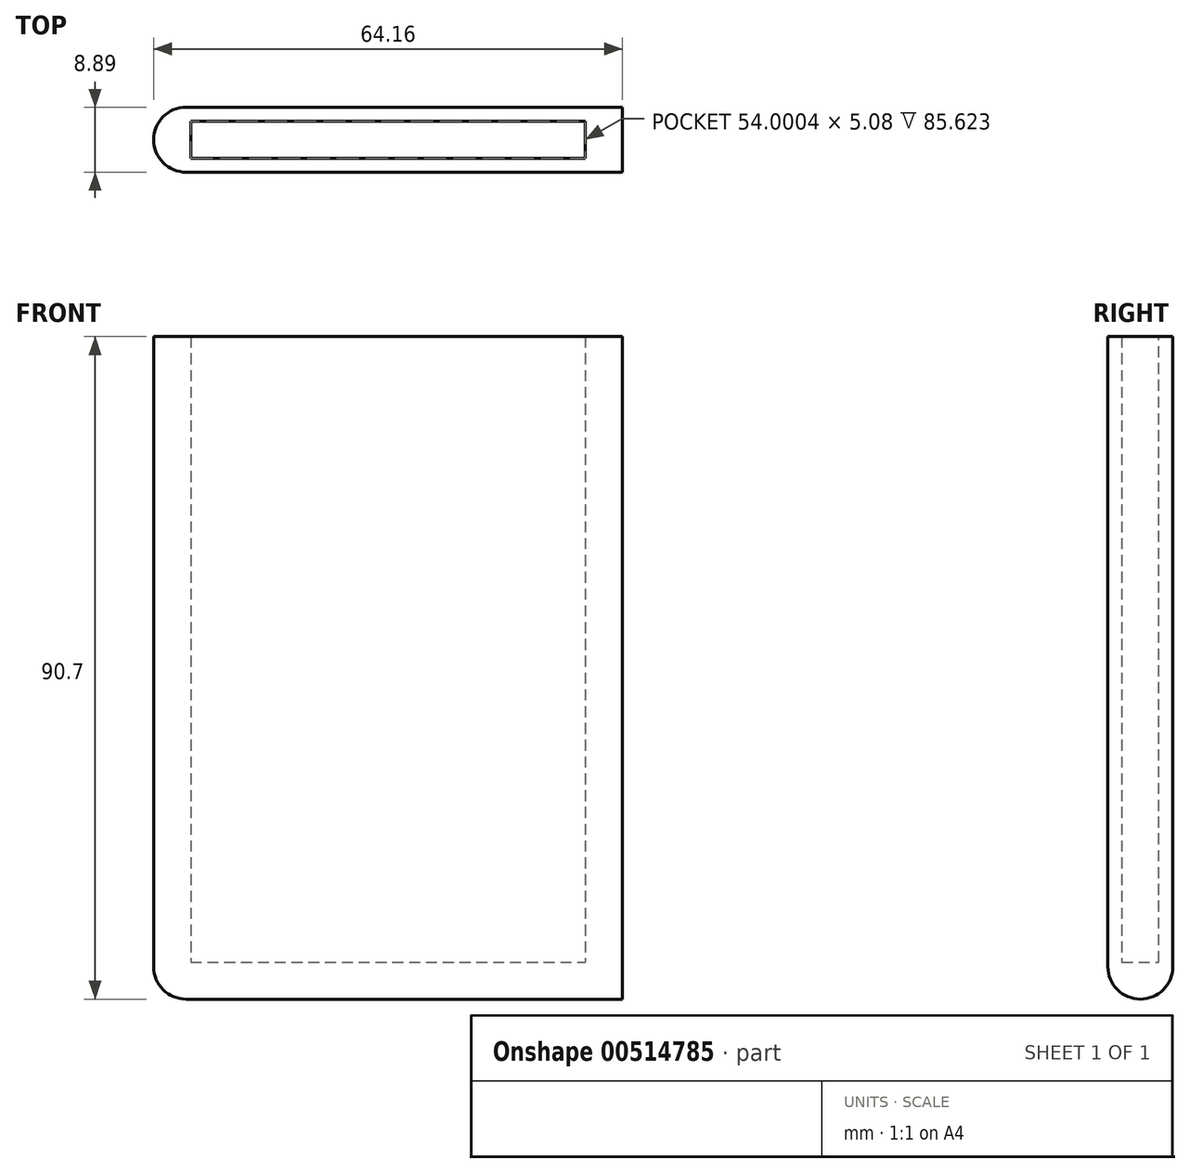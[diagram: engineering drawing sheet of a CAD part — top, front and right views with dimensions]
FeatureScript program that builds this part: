
annotation { "Feature Type Name" : "Feature", "Feature Type Description" : "" }
export const myFeature = defineFeature(function(context is Context, id is Id, definition is map)
    precondition{}
    {
        {
            var Q0;
            Q0=qCreatedBy(makeId("Front.planeOp"),FACE);
            var sketch = newSketch(context, id + "F0", { "sketchPlane" : qUnion([Q0])});
            skLineSegment(sketch, "E0.bottom", {"start": v(0, 0) * mm, "end": v(54, 0) * mm});
            skLineSegment(sketch, "E0.top", {"start": v(0, 85.62) * mm, "end": v(54, 85.62) * mm});
            skLineSegment(sketch, "E0.left", {"start": v(0, 0) * mm, "end": v(0, 85.62) * mm});
            skLineSegment(sketch, "E0.right", {"start": v(54, 0) * mm, "end": v(54, 85.62) * mm});
            skLineSegment(sketch, "E1.0", {"start": v(-5.08, 0) * mm, "end": v(-5.08, 85.62) * mm});
            skLineSegment(sketch, "E2.0", {"start": v(59.08, 0) * mm, "end": v(59.08, 85.62) * mm});
            skLineSegment(sketch, "E3.0", {"start": v(0, -5.08) * mm, "end": v(54, -5.08) * mm});
            skLineSegment(sketch, "E4.top", {"start": v(54, -5.08) * mm, "end": v(59.08, -5.08) * mm});
            skLineSegment(sketch, "E4.right", {"start": v(59.08, 0) * mm, "end": v(59.08, -5.08) * mm});
            skLineSegment(sketch, "E5.bottom", {"start": v(-5.08, 85.62) * mm, "end": v(59.08, 85.62) * mm});
            skLineSegment(sketch, "E5.top", {"start": v(-5.08, -5.08) * mm, "end": v(59.08, -5.08) * mm});
            skLineSegment(sketch, "E5.left", {"start": v(-5.08, 85.62) * mm, "end": v(-5.08, -5.08) * mm});
            skLineSegment(sketch, "E5.right", {"start": v(59.08, 85.62) * mm, "end": v(59.08, -5.08) * mm});
            skSolve(sketch);
        }
        {
            var Q0;
            Q0=makeQuery(id+"F0.imprint","IMPRINT",FACE,{"disambiguationData":[TD([[makeQuery(id+"F0.imprint","IMPRINT",EDGE,{"derivedFrom":sQuery(id+"F0.wireOp",EDGE,"E0.bottom")}),-1.0]])]});
            extrude(context, id + "F1", {"entities" : qUnion([Q0]), "depth" : 6.35 * mm, "offsetDistance" : 25.4 * mm});
        }
        {
            var Q0;
            Q0=makeQuery(id+"F1.opExtrude","CAP_FACE",FACE,{"disambiguationData":[OSD([sQuery(id+"F0.wireOp",EDGE,"E0.bottom"),sQuery(id+"F0.wireOp",EDGE,"E0.left"),sQuery(id+"F0.wireOp",EDGE,"E0.right"),sQuery(id+"F0.wireOp",EDGE,"E5.bottom"),sQuery(id+"F0.wireOp",EDGE,"E5.top"),sQuery(id+"F0.wireOp",EDGE,"E5.left"),sQuery(id+"F0.wireOp",EDGE,"E5.right")])],"isStart":false});
            extrude(context, id + "F2", {"entities" : qUnion([Q0]), "operationType" : NewBodyOperationType.ADD, "depth" : 1.27 * mm, "offsetDistance" : 25.4 * mm});
        }
        {
            var Q0;
            {var subQ0=sQuery(id+"F0.wireOp",EDGE,"E0.right");var subQ3=sQuery(id+"FsMvsPdMRP7UvRH_1.wireOp",EDGE,"BMKbSKOw-1y13-ICIE-zcvO-LVdtaucvQ7qD.top");Q0=makeQuery(id+"F2.boolean.opBoolean","MERGE",FACE,{"derivedFrom":[makeQuery(id+"FD6a4dajuMmCxVc_1.boolean.opBoolean","SPLIT",FACE,{"disambiguationData":[TD([makeQuery(id+"FD6a4dajuMmCxVc_1.opExtrude","SWEPT_FACE",FACE,{"disambiguationData":[OSD([subQ3])]})])],"derivedFrom":makeQuery(id+"F1.opExtrude","SWEPT_FACE",FACE,{"disambiguationData":[OSD([subQ0])]})}),makeQuery(id+"F2.opExtrude","SWEPT_FACE",FACE,{"disambiguationData":[OSD([subQ0])]})]});}
            var sketch = newSketch(context, id + "F3", { "sketchPlane" : qUnion([Q0])});
            skLineSegment(sketch, "E6.bottom", {"start": v(7.62, 85.62) * mm, "end": v(6.35, 85.62) * mm});
            skLineSegment(sketch, "E6.top", {"start": v(7.62, 0) * mm, "end": v(6.35, 0) * mm});
            skLineSegment(sketch, "E6.left", {"start": v(7.62, 85.62) * mm, "end": v(7.62, 0) * mm});
            skLineSegment(sketch, "E6.right", {"start": v(6.35, 85.62) * mm, "end": v(6.35, 0) * mm});
            skSolve(sketch);
        }
        {
            var Q0;
            Q0=makeQuery(id+"F3.imprint","IMPRINT",FACE,{"disambiguationData":[TD([[makeQuery(id+"F3.imprint","IMPRINT",EDGE,{"derivedFrom":sQuery(id+"F3.wireOp",EDGE,"E6.bottom")}),1.0]])]});
            extrude(context, id + "F4", {"entities" : qUnion([Q0]), "operationType" : NewBodyOperationType.ADD, "depth" : 54 * mm, "offsetDistance" : 25.4 * mm});
        }
        {
            var Q0;
            Q0=makeQuery(id+"F1.opExtrude","CAP_FACE",FACE,{"disambiguationData":[OSD([sQuery(id+"F0.wireOp",EDGE,"E0.bottom"),sQuery(id+"F0.wireOp",EDGE,"E0.left"),sQuery(id+"F0.wireOp",EDGE,"E0.right"),sQuery(id+"F0.wireOp",EDGE,"E5.bottom"),sQuery(id+"F0.wireOp",EDGE,"E5.top"),sQuery(id+"F0.wireOp",EDGE,"E5.left"),sQuery(id+"F0.wireOp",EDGE,"E5.right")])],"isStart":true});
            extrude(context, id + "F5", {"entities" : qUnion([Q0]), "operationType" : NewBodyOperationType.ADD, "depth" : 1.27 * mm, "offsetDistance" : 25.4 * mm});
        }
        {
            var Q0;
            {var subQ0=sQuery(id+"F0.wireOp",EDGE,"E0.right");var subQ6=sQuery(id+"FsMvsPdMRP7UvRH_1.wireOp",EDGE,"0TRoBfL0-gIRG-llyi-OvEc-OO58qrmEgHhy.top");Q0=makeQuery(id+"F5.boolean.opBoolean","MERGE",FACE,{"derivedFrom":[makeQuery(id+"FD6a4dajuMmCxVc_1.boolean.opBoolean","SPLIT",FACE,{"disambiguationData":[TD([makeQuery(id+"FD6a4dajuMmCxVc_1.opExtrude","SWEPT_FACE",FACE,{"disambiguationData":[OSD([subQ6])]})])],"derivedFrom":makeQuery(id+"F1.opExtrude","SWEPT_FACE",FACE,{"disambiguationData":[OSD([subQ0])]})}),makeQuery(id+"F5.opExtrude","SWEPT_FACE",FACE,{"disambiguationData":[OSD([subQ0])]})]});}
            var sketch = newSketch(context, id + "F6", { "sketchPlane" : qUnion([Q0])});
            skLineSegment(sketch, "E7.bottom", {"start": v(-1.27, 0) * mm, "end": v(0, 0) * mm});
            skLineSegment(sketch, "E7.top", {"start": v(-1.27, 85.62) * mm, "end": v(0, 85.62) * mm});
            skLineSegment(sketch, "E7.left", {"start": v(-1.27, 0) * mm, "end": v(-1.27, 85.62) * mm});
            skLineSegment(sketch, "E7.right", {"start": v(0, 0) * mm, "end": v(0, 85.62) * mm});
            skSolve(sketch);
        }
        {
            var Q0;
            Q0=makeQuery(id+"F6.imprint","IMPRINT",FACE,{"disambiguationData":[TD([[makeQuery(id+"F6.imprint","IMPRINT",EDGE,{"derivedFrom":sQuery(id+"F6.wireOp",EDGE,"E7.bottom")}),-1.0]])]});
            extrude(context, id + "F7", {"entities" : qUnion([Q0]), "operationType" : NewBodyOperationType.ADD, "depth" : 54 * mm, "offsetDistance" : 25.4 * mm});
        }
        {
            var Q0;
            Q0=makeQuery(id+"F2.opExtrude","CAP_EDGE",EDGE,{"disambiguationData":[OSD([sQuery(id+"F0.wireOp",EDGE,"E5.left")])],"isStart":false});
            var Q1;
            Q1=makeQuery(id+"F5.opExtrude","CAP_EDGE",EDGE,{"disambiguationData":[OSD([sQuery(id+"F0.wireOp",EDGE,"E5.left")])],"isStart":false});
            var Q2;
            Q2=makeQuery(id+"F5.opExtrude","CAP_EDGE",EDGE,{"disambiguationData":[OSD([sQuery(id+"F0.wireOp",EDGE,"E5.right")])],"isStart":false});
            var Q3;
            Q3=makeQuery(id+"F2.opExtrude","CAP_EDGE",EDGE,{"disambiguationData":[OSD([sQuery(id+"F0.wireOp",EDGE,"E5.right")])],"isStart":false});
            var Q4;
            {var subQ0=sQuery(id+"F0.wireOp",EDGE,"E5.left");var subQ1=sQuery(id+"F0.wireOp",EDGE,"E5.top");Q4=makeQuery(id+"F5.boolean.opBoolean","MERGE",EDGE,{"derivedFrom":[makeQuery(id+"F2.boolean.opBoolean","MERGE",EDGE,{"derivedFrom":[makeQuery(id+"F1.opExtrude","SWEPT_EDGE",EDGE,{"disambiguationData":[OSD([subQ1,subQ0])]}),makeQuery(id+"F2.opExtrude","SWEPT_EDGE",EDGE,{"disambiguationData":[OSD([subQ1,subQ0])]})]}),makeQuery(id+"F5.opExtrude","SWEPT_EDGE",EDGE,{"disambiguationData":[OSD([subQ1,subQ0])]})]});}
            var Q5;
            Q5=makeQuery(id+"F5.opExtrude","CAP_EDGE",EDGE,{"disambiguationData":[OSD([sQuery(id+"F0.wireOp",EDGE,"E5.top")])],"isStart":false});
            var Q6;
            Q6=makeQuery(id+"F2.opExtrude","CAP_EDGE",EDGE,{"disambiguationData":[OSD([sQuery(id+"F0.wireOp",EDGE,"E5.top")])],"isStart":false});
            var Q7;
            {var subQ0=sQuery(id+"F0.wireOp",EDGE,"E5.right");var subQ1=sQuery(id+"F0.wireOp",EDGE,"E5.top");Q7=makeQuery(id+"F5.boolean.opBoolean","MERGE",EDGE,{"derivedFrom":[makeQuery(id+"F2.boolean.opBoolean","MERGE",EDGE,{"derivedFrom":[makeQuery(id+"F1.opExtrude","SWEPT_EDGE",EDGE,{"disambiguationData":[OSD([subQ1,subQ0])]}),makeQuery(id+"F2.opExtrude","SWEPT_EDGE",EDGE,{"disambiguationData":[OSD([subQ1,subQ0])]})]}),makeQuery(id+"F5.opExtrude","SWEPT_EDGE",EDGE,{"disambiguationData":[OSD([subQ1,subQ0])]})]});}
            fillet(context, id + "F8", {"entities" : qUnion([Q0, Q1, Q2, Q3, Q4, Q5, Q6, Q7]), "radius" : 4.44 * mm, "tangentPropagation" : true, "allowEdgeOverflow" : false});
        }
        {
            var Q0;
            Q0=makeQuery(id+"F7.opExtrude","SWEPT_FACE",FACE,{"disambiguationData":[OSD([sQuery(id+"F6.wireOp",EDGE,"E7.right")])]});
            extrude(context, id + "F9", {"entities" : qUnion([Q0]), "operationType" : NewBodyOperationType.ADD, "depth" : 0.64 * mm, "offsetDistance" : 25.4 * mm});
        }
        {
            var Q0;
            Q0=makeQuery(id+"F4.opExtrude","SWEPT_FACE",FACE,{"disambiguationData":[OSD([sQuery(id+"F3.wireOp",EDGE,"E6.right")])]});
            extrude(context, id + "F10", {"entities" : qUnion([Q0]), "operationType" : NewBodyOperationType.ADD, "depth" : 0.64 * mm, "offsetDistance" : 25.4 * mm});
        }
    });
